# Revit family: XTe - Escala Gráfica
name_source: partatom
category: Anotaciones genéricas
revit_build: Autodesk Revit 2013 (Build: 20121003_2115(x64)
units: mm (PartAtom-declared; Revit-internal decimal feet)

## types (33) — shared parameters
D1 = 0.01 m
D2 = 0.02 m
D3 = 0.04 m
D4 = 0.08 m

## per-type parameters (varying)
| type | Esc | Escala | N1 | N2 | N3 | N4 |
| 1/0100 | 100 | 100 | 1 | 2 | 4 | 8 |
| 1/0050 | 50 | 50 | 0.5 | 1 | 2 | 4 |
| 1/0075 | 75 | 75 | 0.75 | 1.5 | 3 | 6 |
| 1/0001 | 1 | 1 | 0.01 | 0.02 | 0.04 | 0.08 |
| 1/0005 | 5 | 5 | 0.05 | 0.1 | 0.2 | 0.4 |
| 1/0010 | 10 | 10 | 0.1 | 0.2 | 0.4 | 0.8 |
| 1/0015 | 15 | 15 | 0.15 | 0.3 | 0.6 | 1.2 |
| 1/0020 | 20 | 20 | 0.2 | 0.4 | 0.8 | 1.6 |
| 1/0030 | 30 | 30 | 0.3 | 0.6 | 1.2 | 2.4 |
| 1/0025 | 25 | 25 | 0.25 | 0.5 | 1 | 2 |
| 1/0035 | 35 | 35 | 0.35 | 0.7 | 1.4 | 2.8 |
| 1/0040 | 40 | 40 | 0.4 | 0.8 | 1.6 | 3.2 |
| 1/0125 | 125 | 125 | 1.25 | 2.5 | 5 | 10 |
| 1/0150 | 150 | 150 | 1.5 | 3 | 6 | 12 |
| 1/0200 | 200 | 200 | 2 | 4 | 8 | 16 |
| 1/0250 | 250 | 250 | 2.5 | 5 | 10 | 20 |
| 1/0300 | 300 | 300 | 3 | 6 | 12 | 24 |
| 1/0400 | 400 | 400 | 4 | 8 | 16 | 32 |
| 1/0500 | 500 | 500 | 5 | 10 | 20 | 40 |
| 1/0750 | 750 | 750 | 7.5 | 15 | 30 | 60 |
| 1/1000 | 1000 | 1000 | 10 | 20 | 40 | 80 |
| 1/1200 | 1200 | 1200 | 12 | 24 | 48 | 96 |
| 1/1250 | 1250 | 1250 | 12.5 | 25 | 50 | 100 |
| 1/1300 | 1300 | 1300 | 13 | 26 | 52 | 104 |
| 1/1500 | 1500 | 1500 | 15 | 30 | 60 | 120 |
| 1/1750 | 1750 | 1750 | 17.5 | 35 | 70 | 140 |
| 1/2000 | 2000 | 2000 | 20 | 40 | 80 | 160 |
| 1/2500 | 2500 | 2500 | 25 | 50 | 100 | 200 |
| 1/3000 | 3000 | 3000 | 30 | 60 | 120 | 240 |
| 1/4000 | 4000 | 4000 | 40 | 80 | 160 | 320 |
| 1/5000 | 5000 | 5000 | 50 | 100 | 200 | 400 |
| 1/7500 | 7500 | 7500 | 75 | 150 | 300 | 600 |
| 1/10000 | 10000 | 10000 | 100 | 200 | 400 | 800 |
